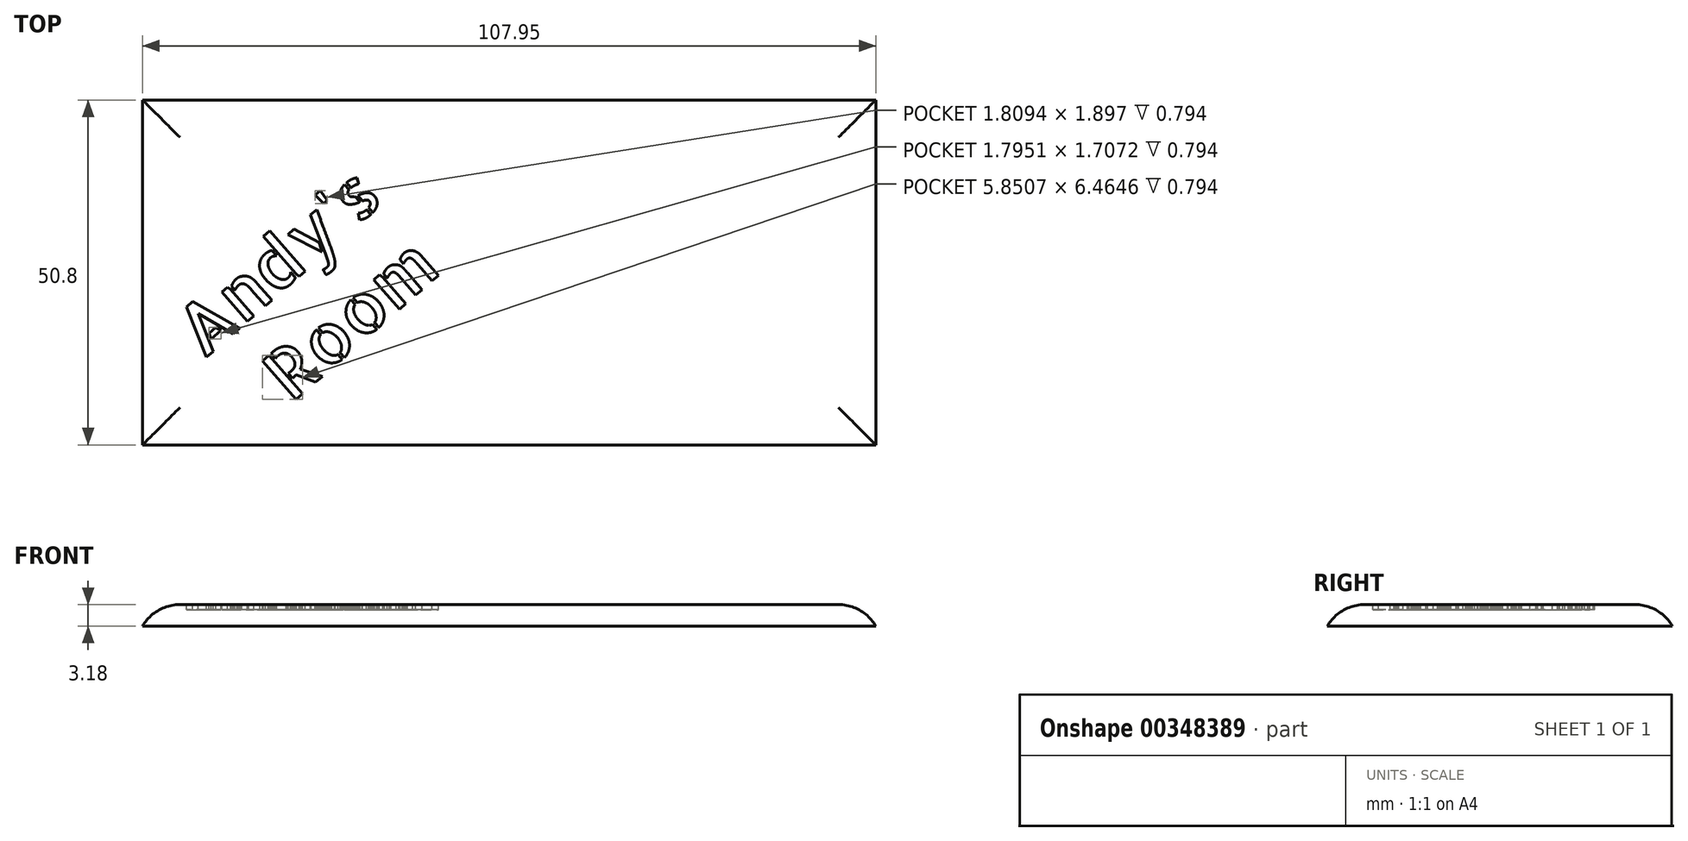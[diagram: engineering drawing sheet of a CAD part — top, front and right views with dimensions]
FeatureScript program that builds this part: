
annotation { "Feature Type Name" : "Feature", "Feature Type Description" : "" }
export const myFeature = defineFeature(function(context is Context, id is Id, definition is map)
    precondition{}
    {
        {
            var Q0;
            Q0=qCreatedBy(makeId("Top.planeOp"),FACE);
            var sketch = newSketch(context, id + "F0", { "sketchPlane" : qUnion([Q0])});
            skLineSegment(sketch, "E0.bottom", {"start": v(-68.37, 37.46) * mm, "end": v(39.58, 37.46) * mm});
            skLineSegment(sketch, "E0.top", {"start": v(-68.37, -13.34) * mm, "end": v(39.58, -13.34) * mm});
            skLineSegment(sketch, "E0.left", {"start": v(-68.37, 37.46) * mm, "end": v(-68.37, -13.34) * mm});
            skLineSegment(sketch, "E0.right", {"start": v(39.58, 37.46) * mm, "end": v(39.58, -13.34) * mm});
            skSolve(sketch);
        }
        {
            var Q0;
            Q0=makeQuery(id+"F0.imprint","IMPRINT",FACE,{"disambiguationData":[TD([[makeQuery(id+"F0.imprint","IMPRINT",EDGE,{"derivedFrom":sQuery(id+"F0.wireOp",EDGE,"E0.bottom")}),-1.0]])]});
            extrude(context, id + "F1", {"entities" : qUnion([Q0]), "depth" : 3.17 * mm});
        }
        {
            var Q0;
            Q0=makeQuery(id+"F1.opExtrude","CAP_EDGE",EDGE,{"disambiguationData":[OSD([sQuery(id+"F0.wireOp",EDGE,"E0.left")])],"isStart":false});
            var Q1;
            Q1=makeQuery(id+"F1.opExtrude","CAP_EDGE",EDGE,{"disambiguationData":[OSD([sQuery(id+"F0.wireOp",EDGE,"E0.bottom")])],"isStart":false});
            var Q2;
            Q2=makeQuery(id+"F1.opExtrude","CAP_EDGE",EDGE,{"disambiguationData":[OSD([sQuery(id+"F0.wireOp",EDGE,"E0.right")])],"isStart":false});
            var Q3;
            Q3=makeQuery(id+"F1.opExtrude","CAP_EDGE",EDGE,{"disambiguationData":[OSD([sQuery(id+"F0.wireOp",EDGE,"E0.top")])],"isStart":false});
            fillet(context, id + "F2", {"entities" : qUnion([Q0, Q1, Q2, Q3]), "radius" : 6.35 * mm, "tangentPropagation" : true, "allowEdgeOverflow" : false});
        }
        {
            var Q0;
            Q0=makeQuery(id+"F1.opExtrude","CAP_FACE",FACE,{"disambiguationData":[OSD([sQuery(id+"F0.wireOp",EDGE,"E0.bottom"),sQuery(id+"F0.wireOp",EDGE,"E0.top"),sQuery(id+"F0.wireOp",EDGE,"E0.left"),sQuery(id+"F0.wireOp",EDGE,"E0.right")])],"isStart":false});
            var sketch = newSketch(context, id + "F3", { "sketchPlane" : qUnion([Q0])});
            skText(sketch, "E1", { "text": "Andy\'s \n  Room", "fontName": "AllertaStencil-Regular.ttf"});
            const initialGuessF3  = {"E1": [-0.05942, -0.0008, 0.75427, 0.65657, 0.00751]};
            skSetInitialGuess(sketch, initialGuessF3);
            skSolve(sketch);
        }
        {
            var Q0;
            Q0 = qSketchRegion(id + "F3", true);
            extrude(context, id + "F4", {"entities" : qUnion([Q0]), "operationType" : NewBodyOperationType.REMOVE, "oppositeDirection" : true, "depth" : 0.8 * mm});
        }
    });
